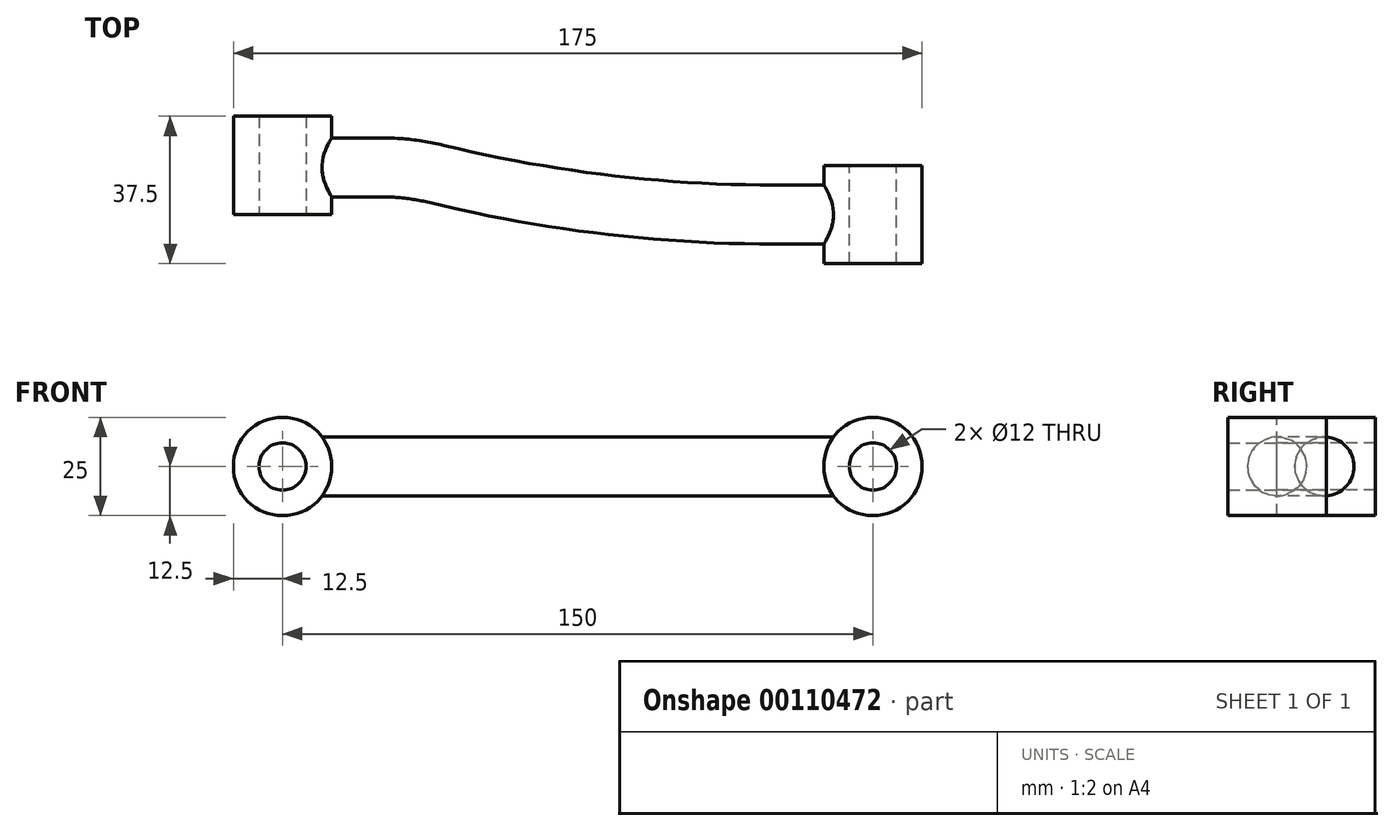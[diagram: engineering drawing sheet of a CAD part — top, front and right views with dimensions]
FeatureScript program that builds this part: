
annotation { "Feature Type Name" : "Feature", "Feature Type Description" : "" }
export const myFeature = defineFeature(function(context is Context, id is Id, definition is map)
    precondition{}
    {
        {
            var Q0;
            Q0=qCreatedBy(makeId("Top.planeOp"),FACE);
            var sketch = newSketch(context, id + "F0", { "sketchPlane" : qUnion([Q0])});
            skLineSegment(sketch, "E0", {"start": v(0, 0) * mm, "end": v(0, 12) * mm, "construction": true});
            skLineSegment(sketch, "E1", {"start": v(0, 12) * mm, "end": v(25, 12) * mm});
            skLineSegment(sketch, "E2", {"start": v(125, 0) * mm, "end": v(150, 0) * mm});
            skArc(sketch, "E3", {"start": v(25, 12) * mm, "mid": v(32.15, 11.57) * mm, "end": v(39.2, 10.3) * mm});
            skArc(sketch, "E4", {"start": v(39.2, 10.3) * mm, "mid": v(81.79, 2.58) * mm, "end": v(125, 0) * mm});
            skSolve(sketch);
        }
        {
            var Q0;
            Q0=qCreatedBy(makeId("Right.planeOp"),FACE);
            var sketch = newSketch(context, id + "F1", { "sketchPlane" : qUnion([Q0])});
            skCircle(sketch, "E5", {"center": v(12, 0) * mm, "radius": 7.5 * mm});
            skSolve(sketch);
        }
        {
            var Q0;
            Q0 = qSketchRegion(id + "F1", true);
            var Q1;
            Q1 = qConstructionFilter(qBodyType(qCreatedBy(id + "F0" ,EDGE), BodyType.WIRE), ConstructionObject.NO);
            sweep(context, id + "F2", {"profiles" : qUnion([Q0]), "path" : qUnion([Q1])});
        }
        {
            var Q0;
            Q0=qCreatedBy(makeId("Front.planeOp"),FACE);
            var sketch = newSketch(context, id + "F3", { "sketchPlane" : qUnion([Q0])});
            skCircle(sketch, "E6", {"center": v(0, 0) * mm, "radius": 6 * mm});
            skCircle(sketch, "E7", {"center": v(0, 0) * mm, "radius": 12.5 * mm});
            skLineSegment(sketch, "E8", {"start": v(0, 0) * mm, "end": v(150, 0) * mm, "construction": true});
            skCircle(sketch, "E9", {"center": v(150, 0) * mm, "radius": 6 * mm});
            skCircle(sketch, "E10", {"center": v(150, 0) * mm, "radius": 12.5 * mm});
            skSolve(sketch);
        }
        {
            var Q0;
            Q0=makeQuery(id+"F3.imprint","IMPRINT",FACE,{"disambiguationData":[TD([[makeQuery(id+"F3.imprint","IMPRINT",EDGE,{"derivedFrom":sQuery(id+"F3.wireOp",EDGE,"E9")}),1.0]])]});
            extrude(context, id + "F4", {"entities" : qUnion([Q0]), "operationType" : NewBodyOperationType.REMOVE, "endBound" : BoundingType.SYMMETRIC, "depth" : 25 * mm});
        }
        {
            var Q0;
            Q0=makeQuery(id+"F3.imprint","IMPRINT",FACE,{"disambiguationData":[TD([[makeQuery(id+"F3.imprint","IMPRINT",EDGE,{"derivedFrom":sQuery(id+"F3.wireOp",EDGE,"E9")}),-1.0]])]});
            extrude(context, id + "F5", {"entities" : qUnion([Q0]), "operationType" : NewBodyOperationType.ADD, "endBound" : BoundingType.SYMMETRIC, "depth" : 25 * mm});
        }
        {
            var Q0;
            Q0=makeQuery(id+"F3.imprint","IMPRINT",FACE,{"disambiguationData":[TD([[makeQuery(id+"F3.imprint","IMPRINT",EDGE,{"derivedFrom":sQuery(id+"F3.wireOp",EDGE,"E6")}),-1.0]])]});
            extrude(context, id + "F6", {"entities" : qUnion([Q0]), "operationType" : NewBodyOperationType.ADD, "oppositeDirection" : true, "depth" : 25 * mm});
        }
        {
            var Q0;
            Q0=makeQuery(id+"F3.imprint","IMPRINT",FACE,{"disambiguationData":[TD([[makeQuery(id+"F3.imprint","IMPRINT",EDGE,{"derivedFrom":sQuery(id+"F3.wireOp",EDGE,"E6")}),1.0]])]});
            extrude(context, id + "F7", {"entities" : qUnion([Q0]), "operationType" : NewBodyOperationType.REMOVE, "endBound" : BoundingType.THROUGH_ALL, "oppositeDirection" : true, "depth" : 25 * mm});
        }
    });
